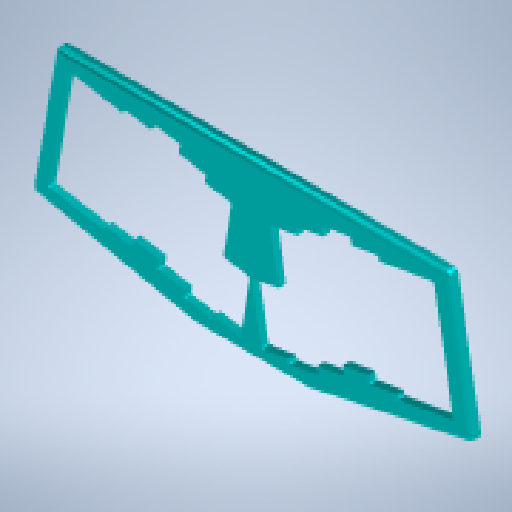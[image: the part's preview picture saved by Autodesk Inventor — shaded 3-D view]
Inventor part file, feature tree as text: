
AUTODESK INVENTOR PART (.ipt)
format: ipt  version: 2023 (Build 270158000, 158)  size: 612,352 bytes
history: native  units: mm
features: reference x45, other x31, sketch x4, extrude x3, fillet x3, hole x1
ambient origin geometry x8: Origin, YZ Plane, XZ Plane, XY Plane, X Axis, Y Axis, Z Axis, Center Point
bodies: Solid1 (feature_tree)
feature tree (87):
  extrude  "Extrusion1"  Depth=9.0mm
  extrude  "Extrusion2"  Depth=9.0mm
  extrude  "Extrusion4"  Depth=1.0mm
  fillet  "Fillet1"  Radius=1.0mm
  fillet  "Fillet2"  Radius=1.0mm
  fillet  "Fillet3"  Radius=1.0mm
  hole  "Hole1"  [1 undecoded]
  sketch  "Sketch1"  dims[d0=9.0mm d1=9.0mm d3=9.0mm]
  reference  "Reference1"
  reference  "Reference2"
  reference  "Reference3"
  reference  "Reference5"
  reference  "Reference6"
  sketch  "Sketch2"  dims[d4=9.0mm d5=9.0mm]
  reference  "Reference7"
  reference  "Reference8"
  reference  "Reference9"
  reference  "Reference10"
  reference  "Reference11"
  reference  "Reference12"
  reference  "Reference13"
  reference  "Reference14"
  reference  "Reference15"
  reference  "Reference16"
  reference  "Reference17"
  reference  "Reference18"
  reference  "Reference19"
  reference  "Reference20"
  reference  "Reference21"
  reference  "Reference22"
  reference  "Reference23"
  reference  "Reference24"
  reference  "Reference25"
  reference  "Reference26"
  reference  "Reference27"
  reference  "Reference28"
  reference  "Reference29"
  reference  "Reference30"
  reference  "Reference31"
  reference  "Reference32"
  reference  "Reference33"
  sketch  "Sketch4"  dims[d6=7.0mm d7=0.0mm d8=1.0mm d9=1.0mm d10=1.0mm d11=1.0mm]
  sketch  "Sketch5"  dims[d12=1.0mm d13=1.0mm d14=1.0mm d15=1.0mm d16=1.0mm d17=1.0mm d18=1.0mm d19=1.0mm d20=1.0mm d21=1.0mm d22=1.0mm d23=1.0mm d24=1.0mm d25=1.0mm d26=1.0mm d27=1.0mm d28=1.0mm d32=1.0mm d33=1.0mm d34=1.0mm d35=0.0mm d36=0.0mm d40=2.0mm d41=0.0mm d43=4.0mm d44=4.0mm d45=1.0mm d46=2.0mm d47=6.0mm d48=4.0mm d49=8.0mm d50=90.0deg d51=4.0mm d52=20.594885mm d53=9.0mm d55=9.0mm]
  reference  "Reference98"
  reference  "Reference99"
  reference  "Reference100"
  reference  "Reference101"
  reference  "Reference102"
  reference  "Reference103"
  reference  "Reference104"
  reference  "Reference105"
  reference  "Reference106"
  reference  "Reference107"
  reference  "Reference109"
  reference  "Reference110"
  reference  "Reference111"
  other  "<userpath>\Documents\Inventor\atreus-52\Assembly.iam"
  other  "Assembly.iam"
  other  "switch-plates:1"
  other  "bottom-case:1"
  other  "DSA 1u:1"
  other  "DSA 1u:8"
  other  "DSA 1u:9"
  other  "DSA 1u:16"
  other  "DSA 1u:17"
  other  "DSA 1u:24"
  other  "DSA 1u:26"
  other  "DSA 1u:25"
  other  "DSA 1u:21"
  other  "DSA 1u:20"
  other  "DSA 1u:13"
  other  "DSA 1u:12"
  other  "DSA 1u:5"
  other  "DSA 1u:4"
  other  "DSA 1u:52"
  other  "DSA 1u:47"
  other  "DSA 1u:46"
  other  "DSA 1u:39"
  other  "DSA 1u:38"
  other  "DSA 1u:31"
  other  "DSA 1u:30"
  other  "DSA 1u:27"
  other  "DSA 1u:34"
  other  "DSA 1u:35"
  other  "DSA 1u:42"
  other  "DSA 1u:43"
  other  "DSA 1u:50"
note: 1 required parameter value undecoded (feature->parameter linkage not recoverable at this tier; creation-order binding heuristic only, values carry confidence <= 0.55)
